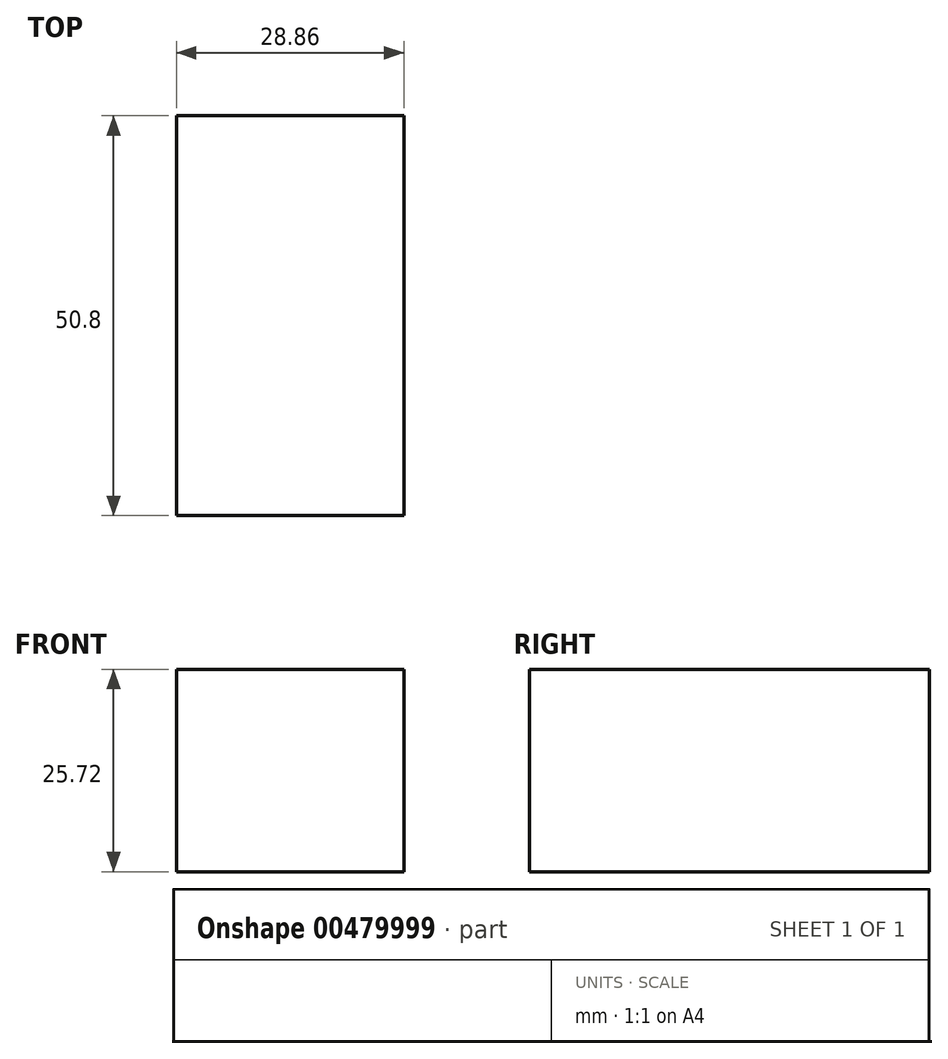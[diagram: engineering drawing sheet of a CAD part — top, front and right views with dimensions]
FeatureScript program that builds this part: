
annotation { "Feature Type Name" : "Feature", "Feature Type Description" : "" }
export const myFeature = defineFeature(function(context is Context, id is Id, definition is map)
    precondition{}
    {
        {
            var Q0;
            Q0=qCreatedBy(makeId("Front.planeOp"),FACE);
            var sketch = newSketch(context, id + "F0", { "sketchPlane" : qUnion([Q0])});
            skLineSegment(sketch, "E0.bottom", {"start": v(-117.8, 13.53) * mm, "end": v(-88.93, 13.53) * mm});
            skLineSegment(sketch, "E0.top", {"start": v(-117.8, -12.19) * mm, "end": v(-88.93, -12.19) * mm});
            skLineSegment(sketch, "E0.left", {"start": v(-117.8, 13.53) * mm, "end": v(-117.8, -12.19) * mm});
            skLineSegment(sketch, "E0.right", {"start": v(-88.93, 13.53) * mm, "end": v(-88.93, -12.19) * mm});
            skSolve(sketch);
        }
        {
            var Q0;
            Q0=makeQuery(id+"F0.imprint","IMPRINT",FACE,{"disambiguationData":[TD([[makeQuery(id+"F0.imprint","IMPRINT",EDGE,{"derivedFrom":sQuery(id+"F0.wireOp",EDGE,"E0.bottom")}),-1.0]])]});
            extrude(context, id + "F1", {"entities" : qUnion([Q0]), "depth" : 50.8 * mm});
        }
    });
